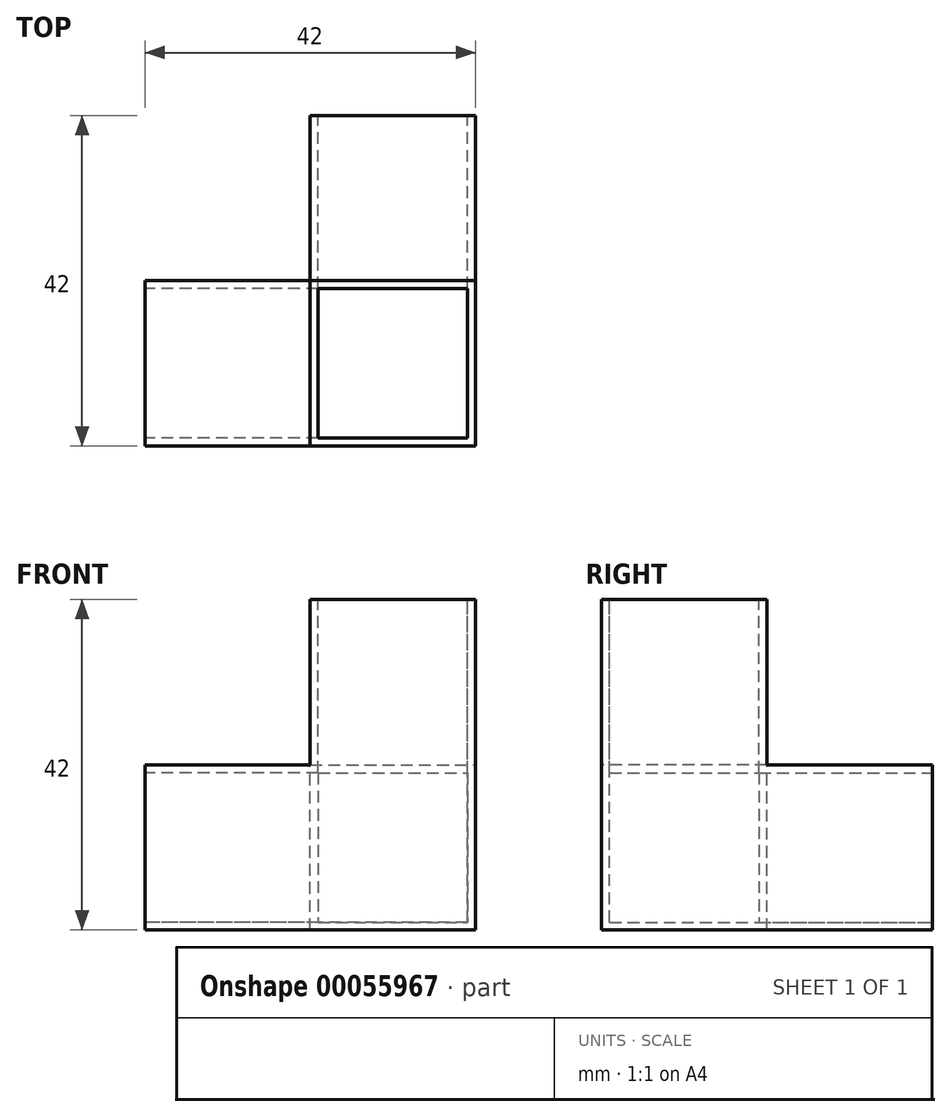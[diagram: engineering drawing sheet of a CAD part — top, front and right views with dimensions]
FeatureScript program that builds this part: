
annotation { "Feature Type Name" : "Feature", "Feature Type Description" : "" }
export const myFeature = defineFeature(function(context is Context, id is Id, definition is map)
    precondition{}
    {
        {
            var Q0;
            Q0=qCreatedBy(makeId("Top.planeOp"),FACE);
            var sketch = newSketch(context, id + "F0", { "sketchPlane" : qUnion([Q0])});
            skLineSegment(sketch, "E0.rect.bottom", {"start": v(21, 21) * mm, "end": v(-21, 21) * mm});
            skLineSegment(sketch, "E0.rect.top", {"start": v(21, -21) * mm, "end": v(-21, -21) * mm});
            skLineSegment(sketch, "E0.rect.left", {"start": v(21, 21) * mm, "end": v(21, -21) * mm});
            skLineSegment(sketch, "E0.rect.right", {"start": v(-21, 21) * mm, "end": v(-21, -21) * mm});
            skPoint(sketch, "E0.rect.middle", {"position": v(0, 0) * mm});
            skSolve(sketch);
        }
        {
            var Q0;
            Q0=makeQuery(id+"F0.imprint","IMPRINT",FACE,{"disambiguationData":[TD([[makeQuery(id+"F0.imprint","IMPRINT",EDGE,{"derivedFrom":sQuery(id+"F0.wireOp",EDGE,"E0.rect.bottom")}),1.0]])]});
            extrude(context, id + "F1", {"entities" : qUnion([Q0]), "depth" : 42 * mm});
        }
        {
            var Q0;
            Q0=makeQuery(id+"F1.opExtrude","CAP_FACE",FACE,{"disambiguationData":[OSD([sQuery(id+"F0.wireOp",EDGE,"E0.rect.bottom"),sQuery(id+"F0.wireOp",EDGE,"E0.rect.top"),sQuery(id+"F0.wireOp",EDGE,"E0.rect.left"),sQuery(id+"F0.wireOp",EDGE,"E0.rect.right")])],"isStart":false});
            var sketch = newSketch(context, id + "F2", { "sketchPlane" : qUnion([Q0])});
            skLineSegment(sketch, "E1.bottom", {"start": v(-21, 21) * mm, "end": v(0, 21) * mm});
            skLineSegment(sketch, "E1.top", {"start": v(-21, 0) * mm, "end": v(0, 0) * mm});
            skLineSegment(sketch, "E1.left", {"start": v(-21, 21) * mm, "end": v(-21, 0) * mm});
            skLineSegment(sketch, "E1.right", {"start": v(0, 21) * mm, "end": v(0, 0) * mm});
            skSolve(sketch);
        }
        {
            var Q0;
            Q0=makeQuery(id+"F2.imprint","IMPRINT",FACE,{"disambiguationData":[TD([[makeQuery(id+"F2.imprint","IMPRINT",EDGE,{"derivedFrom":sQuery(id+"F2.wireOp",EDGE,"E1.bottom")}),1.0]])]});
            extrude(context, id + "F3", {"entities" : qUnion([Q0]), "operationType" : NewBodyOperationType.REMOVE, "endBound" : BoundingType.UP_TO_NEXT, "oppositeDirection" : true, "depth" : 25 * mm});
        }
        {
            var Q0;
            Q0=makeQuery(id+"F1.opExtrude","SWEPT_FACE",FACE,{"disambiguationData":[OSD([sQuery(id+"F0.wireOp",EDGE,"E0.rect.top")])]});
            var sketch = newSketch(context, id + "F4", { "sketchPlane" : qUnion([Q0])});
            skLineSegment(sketch, "E2.bottom", {"start": v(-21, 42) * mm, "end": v(0, 42) * mm});
            skLineSegment(sketch, "E2.top", {"start": v(-21, 21) * mm, "end": v(0, 21) * mm});
            skLineSegment(sketch, "E2.left", {"start": v(-21, 42) * mm, "end": v(-21, 21) * mm});
            skLineSegment(sketch, "E2.right", {"start": v(0, 42) * mm, "end": v(0, 21) * mm});
            skSolve(sketch);
        }
        {
            var Q0;
            Q0=makeQuery(id+"F4.imprint","IMPRINT",FACE,{"disambiguationData":[TD([[makeQuery(id+"F4.imprint","IMPRINT",EDGE,{"derivedFrom":sQuery(id+"F4.wireOp",EDGE,"E2.bottom")}),1.0]])]});
            extrude(context, id + "F5", {"entities" : qUnion([Q0]), "operationType" : NewBodyOperationType.REMOVE, "endBound" : BoundingType.UP_TO_NEXT, "oppositeDirection" : true, "depth" : 25 * mm});
        }
        {
            var Q0;
            Q0=makeQuery(id+"F1.opExtrude","SWEPT_FACE",FACE,{"disambiguationData":[OSD([sQuery(id+"F0.wireOp",EDGE,"E0.rect.left")])]});
            var sketch = newSketch(context, id + "F6", { "sketchPlane" : qUnion([Q0])});
            skLineSegment(sketch, "E3.bottom", {"start": v(21, 42) * mm, "end": v(0, 42) * mm});
            skLineSegment(sketch, "E3.top", {"start": v(21, 21) * mm, "end": v(0, 21) * mm});
            skLineSegment(sketch, "E3.left", {"start": v(21, 42) * mm, "end": v(21, 21) * mm});
            skLineSegment(sketch, "E3.right", {"start": v(0, 42) * mm, "end": v(0, 21) * mm});
            skSolve(sketch);
        }
        {
            var Q0;
            Q0=makeQuery(id+"F6.imprint","IMPRINT",FACE,{"disambiguationData":[TD([[makeQuery(id+"F6.imprint","IMPRINT",EDGE,{"derivedFrom":sQuery(id+"F6.wireOp",EDGE,"E3.bottom")}),1.0]])]});
            extrude(context, id + "F7", {"entities" : qUnion([Q0]), "operationType" : NewBodyOperationType.REMOVE, "endBound" : BoundingType.UP_TO_NEXT, "oppositeDirection" : true, "depth" : 25 * mm});
        }
        {
            var Q0;
            Q0=makeQuery(id+"F1.opExtrude","CAP_FACE",FACE,{"disambiguationData":[OSD([sQuery(id+"F0.wireOp",EDGE,"E0.rect.bottom"),sQuery(id+"F0.wireOp",EDGE,"E0.rect.top"),sQuery(id+"F0.wireOp",EDGE,"E0.rect.left"),sQuery(id+"F0.wireOp",EDGE,"E0.rect.right")])],"isStart":false});
            var sketch = newSketch(context, id + "F8", { "sketchPlane" : qUnion([Q0])});
            skLineSegment(sketch, "E4", {"start": v(0, -21) * mm, "end": v(21, 0) * mm, "construction": true});
            skLineSegment(sketch, "E5.rect.bottom", {"start": v(20, -20) * mm, "end": v(1, -20) * mm});
            skLineSegment(sketch, "E5.rect.top", {"start": v(20, -1) * mm, "end": v(1, -1) * mm});
            skLineSegment(sketch, "E5.rect.left", {"start": v(20, -20) * mm, "end": v(20, -1) * mm});
            skLineSegment(sketch, "E5.rect.right", {"start": v(1, -20) * mm, "end": v(1, -1) * mm});
            skPoint(sketch, "E5.rect.middle", {"position": v(10.5, -10.5) * mm});
            skSolve(sketch);
        }
        {
            var Q0;
            Q0=makeQuery(id+"F8.imprint","IMPRINT",FACE,{"disambiguationData":[TD([[makeQuery(id+"F8.imprint","IMPRINT",EDGE,{"derivedFrom":sQuery(id+"F8.wireOp",EDGE,"E5.rect.bottom")}),-1.0]])]});
            extrude(context, id + "F9", {"entities" : qUnion([Q0]), "operationType" : NewBodyOperationType.REMOVE, "oppositeDirection" : true, "depth" : 41 * mm});
        }
        {
            var Q0;
            Q0=makeQuery(id+"F1.opExtrude","SWEPT_FACE",FACE,{"disambiguationData":[OSD([sQuery(id+"F0.wireOp",EDGE,"E0.rect.right")])]});
            var sketch = newSketch(context, id + "F10", { "sketchPlane" : qUnion([Q0])});
            skLineSegment(sketch, "E6", {"start": v(0, 0) * mm, "end": v(21, 21) * mm, "construction": true});
            skLineSegment(sketch, "E7.rect.bottom", {"start": v(20, 1) * mm, "end": v(1, 1) * mm});
            skLineSegment(sketch, "E7.rect.top", {"start": v(20, 20) * mm, "end": v(1, 20) * mm});
            skLineSegment(sketch, "E7.rect.left", {"start": v(20, 1) * mm, "end": v(20, 20) * mm});
            skLineSegment(sketch, "E7.rect.right", {"start": v(1, 1) * mm, "end": v(1, 20) * mm});
            skPoint(sketch, "E7.rect.middle", {"position": v(10.5, 10.5) * mm});
            skSolve(sketch);
        }
        {
            var Q0;
            Q0=makeQuery(id+"F10.imprint","IMPRINT",FACE,{"disambiguationData":[TD([[makeQuery(id+"F10.imprint","IMPRINT",EDGE,{"derivedFrom":sQuery(id+"F10.wireOp",EDGE,"E7.rect.bottom")}),-1.0]])]});
            extrude(context, id + "F11", {"entities" : qUnion([Q0]), "operationType" : NewBodyOperationType.REMOVE, "oppositeDirection" : true, "depth" : 41 * mm});
        }
        {
            var Q0;
            Q0=makeQuery(id+"F1.opExtrude","SWEPT_FACE",FACE,{"disambiguationData":[OSD([sQuery(id+"F0.wireOp",EDGE,"E0.rect.bottom")])]});
            var sketch = newSketch(context, id + "F12", { "sketchPlane" : qUnion([Q0])});
            skLineSegment(sketch, "E8", {"start": v(-21, 21) * mm, "end": v(0, 0) * mm, "construction": true});
            skLineSegment(sketch, "E9.rect.bottom", {"start": v(-1, 20) * mm, "end": v(-20, 20) * mm});
            skLineSegment(sketch, "E9.rect.top", {"start": v(-1, 1) * mm, "end": v(-20, 1) * mm});
            skLineSegment(sketch, "E9.rect.left", {"start": v(-1, 20) * mm, "end": v(-1, 1) * mm});
            skLineSegment(sketch, "E9.rect.right", {"start": v(-20, 20) * mm, "end": v(-20, 1) * mm});
            skPoint(sketch, "E9.rect.middle", {"position": v(-10.5, 10.5) * mm});
            skSolve(sketch);
        }
        {
            var Q0;
            Q0=makeQuery(id+"F12.imprint","IMPRINT",FACE,{"disambiguationData":[TD([[makeQuery(id+"F12.imprint","IMPRINT",EDGE,{"derivedFrom":sQuery(id+"F12.wireOp",EDGE,"E9.rect.bottom")}),1.0]])]});
            extrude(context, id + "F13", {"entities" : qUnion([Q0]), "operationType" : NewBodyOperationType.REMOVE, "oppositeDirection" : true, "depth" : 41 * mm});
        }
    });
